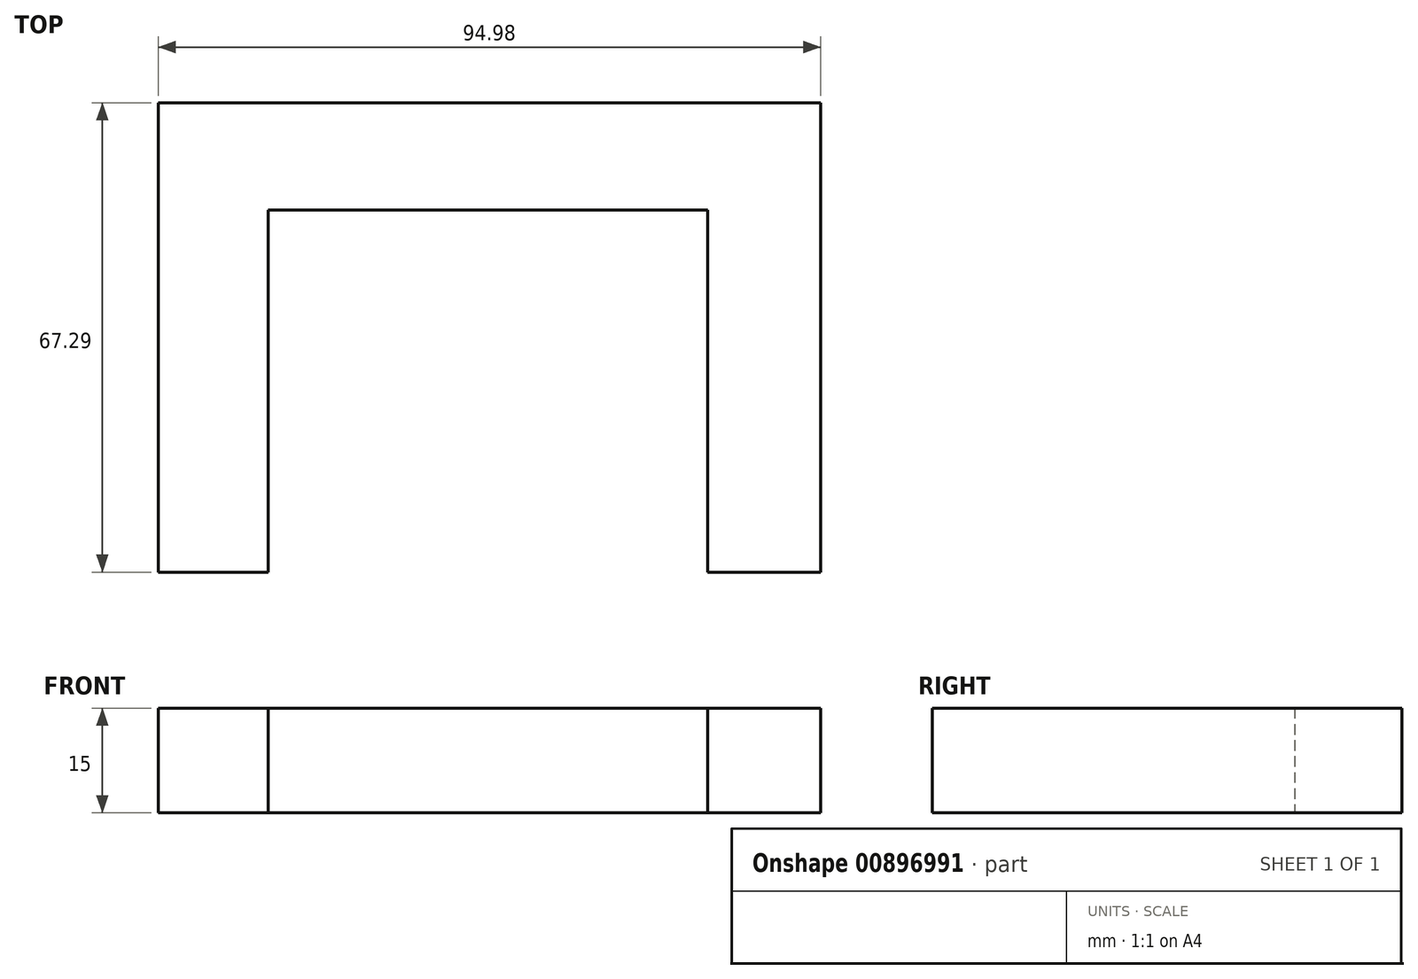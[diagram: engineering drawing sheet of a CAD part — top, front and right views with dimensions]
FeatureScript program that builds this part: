
annotation { "Feature Type Name" : "Feature", "Feature Type Description" : "" }
export const myFeature = defineFeature(function(context is Context, id is Id, definition is map)
    precondition{}
    {
        {
            var Q0;
            Q0=qCreatedBy(makeId("Top.planeOp"),FACE);
            var sketch = newSketch(context, id + "F0", { "sketchPlane" : qUnion([Q0])});
            skPoint(sketch, "E0.middle", {"position": v(0, 0) * mm});
            skLineSegment(sketch, "E1.bottom", {"start": v(-47.6, 0) * mm, "end": v(-31.86, 0) * mm});
            skLineSegment(sketch, "E1.top", {"start": v(-47.6, -51.9) * mm, "end": v(-31.86, -51.9) * mm});
            skLineSegment(sketch, "E1.left", {"start": v(-47.6, 0) * mm, "end": v(-47.6, -51.9) * mm});
            skLineSegment(sketch, "E1.right", {"start": v(-31.86, 0) * mm, "end": v(-31.86, -51.9) * mm});
            skLineSegment(sketch, "E2.bottom", {"start": v(-47.6, 0) * mm, "end": v(47.37, 0) * mm});
            skLineSegment(sketch, "E2.top", {"start": v(-47.6, 15.4) * mm, "end": v(47.37, 15.4) * mm});
            skLineSegment(sketch, "E2.left", {"start": v(-47.6, 0) * mm, "end": v(-47.6, 15.4) * mm});
            skLineSegment(sketch, "E2.right", {"start": v(47.37, 0) * mm, "end": v(47.37, 15.4) * mm});
            skLineSegment(sketch, "E3.bottom", {"start": v(47.37, 0) * mm, "end": v(31.14, 0) * mm});
            skLineSegment(sketch, "E3.top", {"start": v(47.37, -51.9) * mm, "end": v(31.14, -51.9) * mm});
            skLineSegment(sketch, "E3.left", {"start": v(47.37, 0) * mm, "end": v(47.37, -51.9) * mm});
            skLineSegment(sketch, "E3.right", {"start": v(31.14, 0) * mm, "end": v(31.14, -51.9) * mm});
            skSolve(sketch);
        }
        {
            var Q0;
            Q0 = qSketchRegion(id + "F0", true);
            extrude(context, id + "F1", {"entities" : qUnion([Q0]), "depth" : 15 * mm, "offsetDistance" : 25 * mm});
        }
    });
